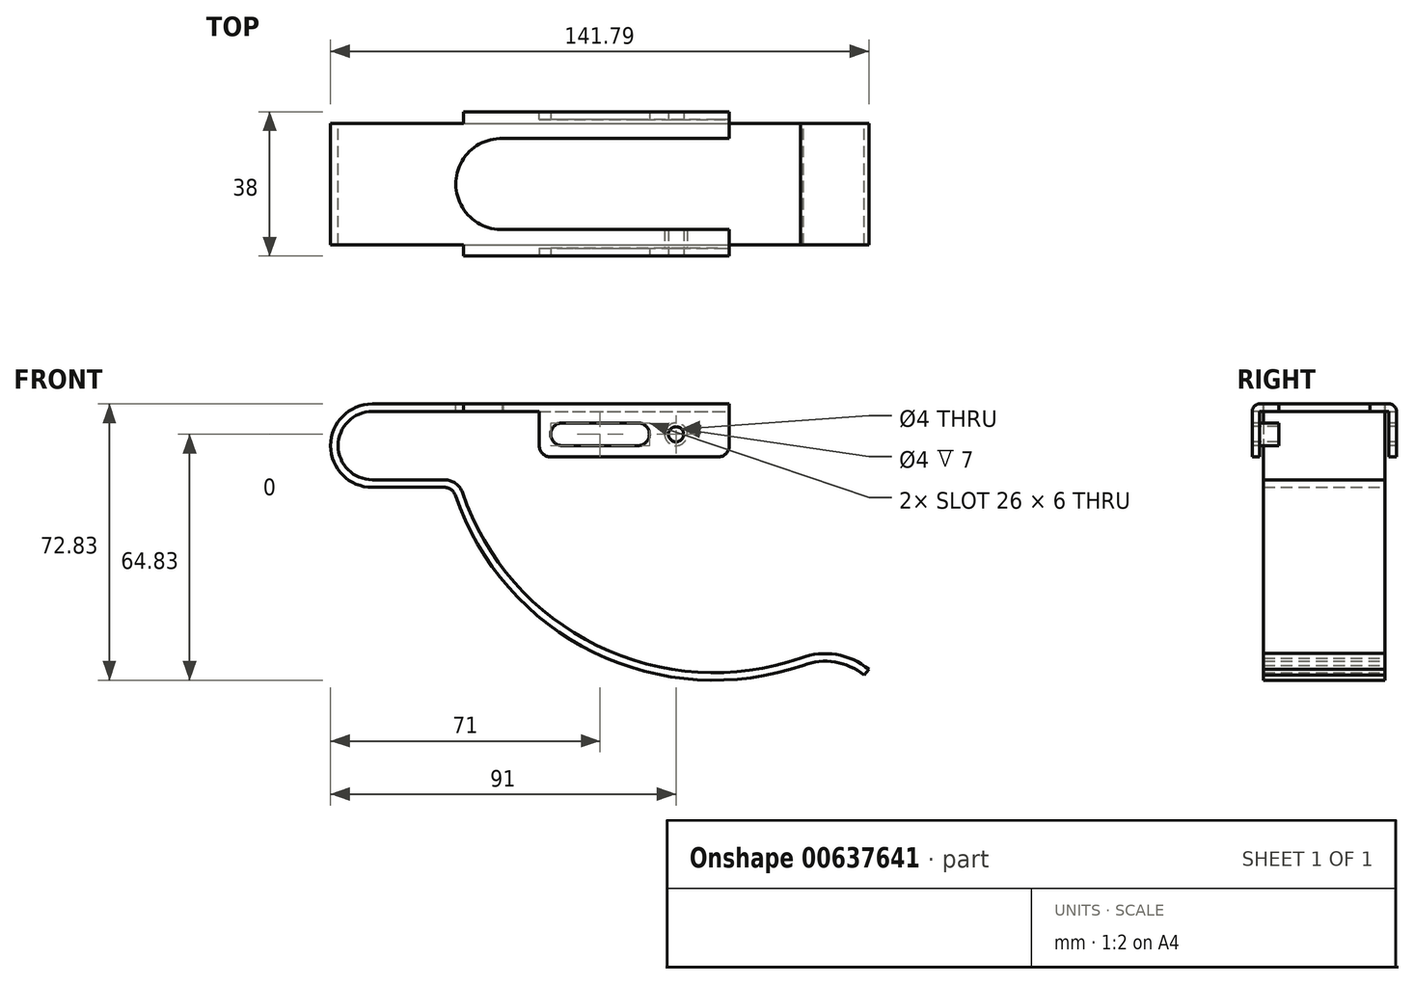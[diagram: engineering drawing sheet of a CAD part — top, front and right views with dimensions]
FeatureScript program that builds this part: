
annotation { "Feature Type Name" : "Feature", "Feature Type Description" : "" }
export const myFeature = defineFeature(function(context is Context, id is Id, definition is map)
    precondition{}
    {
        {
            var Q0;
            Q0=qCreatedBy(makeId("Front.planeOp"),FACE);
            var sketch = newSketch(context, id + "F0", { "sketchPlane" : qUnion([Q0])});
            skArc(sketch, "E0", {"start": v(0, 9) * mm, "mid": v(-9, 0) * mm, "end": v(0, -9) * mm});
            skLineSegment(sketch, "E1", {"start": v(0, 9) * mm, "end": v(94, 9) * mm});
            skLineSegment(sketch, "E2", {"start": v(0, -9) * mm, "end": v(19, -9) * mm});
            skArc(sketch, "E3", {"start": v(23.73, -12.39) * mm, "mid": v(59.23, -52.7) * mm, "end": v(112.85, -56) * mm});
            skArc(sketch, "E4", {"start": v(130.79, -59) * mm, "mid": v(122.23, -55.07) * mm, "end": v(112.85, -56) * mm});
            skPoint(sketch, "E5.visualSharp", {"position": v(22.67, -9) * mm});
            skArc(sketch, "E5.filletArc", {"start": v(23.73, -12.39) * mm, "mid": v(21.91, -9.93) * mm, "end": v(19, -9) * mm});
            skLineSegment(sketch, "E6.0", {"start": v(0, 11) * mm, "end": v(94, 11) * mm});
            skArc(sketch, "E6.1", {"start": v(0, 11) * mm, "mid": v(-11, 0) * mm, "end": v(0, -11) * mm});
            skArc(sketch, "E6.2", {"start": v(129.5, -60.53) * mm, "mid": v(121.88, -57.04) * mm, "end": v(113.53, -57.88) * mm});
            skArc(sketch, "E6.3", {"start": v(21.84, -13.03) * mm, "mid": v(58.37, -54.51) * mm, "end": v(113.53, -57.88) * mm});
            skArc(sketch, "E6.4", {"start": v(21.84, -13.03) * mm, "mid": v(20.75, -11.56) * mm, "end": v(19, -11) * mm});
            skLineSegment(sketch, "E6.5", {"start": v(0, -11) * mm, "end": v(19, -11) * mm});
            skLineSegment(sketch, "E7", {"start": v(129.5, -60.53) * mm, "end": v(130.79, -59) * mm});
            skLineSegment(sketch, "E8", {"start": v(94, 11) * mm, "end": v(94, 9) * mm});
            skLineSegment(sketch, "E9", {"start": v(130.79, -59) * mm, "end": v(133.98, -59) * mm, "construction": true});
            skSolve(sketch);
        }
        {
            var Q0;
            Q0 = qSketchRegion(id + "F0", true);
            extrude(context, id + "F1", {"entities" : qUnion([Q0]), "depth" : 16 * mm, "offsetDistance" : 25 * mm});
        }
        {
            var Q0;
            Q0=makeQuery(id+"F1.opExtrude","SWEPT_FACE",FACE,{"disambiguationData":[OSD([sQuery(id+"F0.wireOp",EDGE,"E6.0")])]});
            var sketch = newSketch(context, id + "F2", { "sketchPlane" : qUnion([Q0])});
            skLineSegment(sketch, "E10.bottom", {"start": v(24, -16) * mm, "end": v(94, -16) * mm});
            skLineSegment(sketch, "E10.top", {"start": v(24, -19) * mm, "end": v(94, -19) * mm});
            skLineSegment(sketch, "E10.left", {"start": v(24, -16) * mm, "end": v(24, -19) * mm});
            skLineSegment(sketch, "E10.right", {"start": v(94, -16) * mm, "end": v(94, -19) * mm});
            skSolve(sketch);
        }
        {
            var Q0;
            Q0 = qSketchRegion(id + "F2", true);
            extrude(context, id + "F3", {"entities" : qUnion([Q0]), "operationType" : NewBodyOperationType.ADD, "oppositeDirection" : true, "depth" : 2 * mm, "offsetDistance" : 25 * mm});
        }
        {
            var Q0;
            Q0=makeQuery(id+"F3.opExtrude","SWEPT_FACE",FACE,{"disambiguationData":[OSD([sQuery(id+"F2.wireOp",EDGE,"E10.top")])]});
            var sketch = newSketch(context, id + "F4", { "sketchPlane" : qUnion([Q0])});
            skLineSegment(sketch, "E11.bottom", {"start": v(94, 11) * mm, "end": v(44, 11) * mm});
            skLineSegment(sketch, "E11.top", {"start": v(94, -3) * mm, "end": v(44, -3) * mm});
            skLineSegment(sketch, "E11.left", {"start": v(94, 11) * mm, "end": v(94, -3) * mm});
            skLineSegment(sketch, "E11.right", {"start": v(44, 11) * mm, "end": v(44, -3) * mm});
            skSolve(sketch);
        }
        {
            var Q0;
            Q0 = qSketchRegion(id + "F4", true);
            extrude(context, id + "F5", {"entities" : qUnion([Q0]), "operationType" : NewBodyOperationType.ADD, "oppositeDirection" : true, "depth" : 2 * mm, "offsetDistance" : 25 * mm});
        }
        {
            var Q0;
            Q0=makeQuery(id+"F3.opExtrude","CAP_EDGE",EDGE,{"disambiguationData":[OSD([sQuery(id+"F2.wireOp",EDGE,"E10.top")])],"isStart":true});
            fillet(context, id + "F6", {"entities" : qUnion([Q0]), "radius" : 2 * mm, "tangentPropagation" : true, "allowEdgeOverflow" : false});
        }
        {
            var Q0;
            Q0=makeQuery(id+"F1.opExtrude","SWEPT_BODY",BODY,{"disambiguationData":[OSD([sQuery(id+"F0.wireOp",EDGE,"E0"),sQuery(id+"F0.wireOp",EDGE,"E1"),sQuery(id+"F0.wireOp",EDGE,"E2"),sQuery(id+"F0.wireOp",EDGE,"E3"),sQuery(id+"F0.wireOp",EDGE,"E4"),sQuery(id+"F0.wireOp",EDGE,"E5.filletArc"),sQuery(id+"F0.wireOp",EDGE,"E6.0"),sQuery(id+"F0.wireOp",EDGE,"E6.1"),sQuery(id+"F0.wireOp",EDGE,"E6.2"),sQuery(id+"F0.wireOp",EDGE,"E6.3"),sQuery(id+"F0.wireOp",EDGE,"E6.4"),sQuery(id+"F0.wireOp",EDGE,"E6.5"),sQuery(id+"F0.wireOp",EDGE,"E7"),sQuery(id+"F0.wireOp",EDGE,"E8")])]});
            var Q1;
            Q1=qCreatedBy(makeId("Front.planeOp"),FACE);
            mirror(context, id + "F7", {"operationType" : NewBodyOperationType.ADD, "entities" : qUnion([Q0]), "mirrorPlane" : qUnion([Q1])});
        }
        {
            var Q0;
            {var subQ0=makeQuery(id+"F3.boolean.opBoolean","MERGE",FACE,{"derivedFrom":[makeQuery(id+"F1.opExtrude","SWEPT_FACE",FACE,{"disambiguationData":[OSD([sQuery(id+"F0.wireOp",EDGE,"E6.0")])]}),makeQuery(id+"F3.opExtrude","CAP_FACE",FACE,{"disambiguationData":[OSD([sQuery(id+"F2.wireOp",EDGE,"E10.bottom"),sQuery(id+"F2.wireOp",EDGE,"E10.top"),sQuery(id+"F2.wireOp",EDGE,"E10.left"),sQuery(id+"F2.wireOp",EDGE,"E10.right")])],"isStart":true})]});Q0=makeQuery(id+"F7.boolean.opBoolean","MERGE",FACE,{"derivedFrom":[subQ0,makeQuery(id+"F7.opPattern","COPY",FACE,{"derivedFrom":subQ0,"instanceName":"1"})]});}
            var sketch = newSketch(context, id + "F8", { "sketchPlane" : qUnion([Q0])});
            skArc(sketch, "E12", {"start": v(34.3, 12) * mm, "mid": v(22, -0.11) * mm, "end": v(34.54, -11.99) * mm});
            skLineSegment(sketch, "E13", {"start": v(33.7, 12) * mm, "end": v(94, 12) * mm});
            skLineSegment(sketch, "E14", {"start": v(34.54, -11.99) * mm, "end": v(94, -11.99) * mm});
            skSolve(sketch);
        }
        {
            var Q0;
            Q0 = qSketchRegion(id + "F8", true);
            var Q1;
            {var subQ0=sQuery(id+"F8.wireOp",EDGE,"E14");Q1=makeQuery(id+"F8.imprint","IMPRINT",FACE,{"disambiguationData":[TD([[makeQuery(id+"F8.imprint","IMPRINT",EDGE,{"derivedFrom":subQ0}),1.0]])]});}
            extrude(context, id + "F9", {"entities" : qUnion([Q0, Q1]), "operationType" : NewBodyOperationType.REMOVE, "oppositeDirection" : true, "depth" : 2 * mm, "offsetDistance" : 25 * mm});
        }
        {
            var Q0;
            Q0=makeQuery(id+"F5.boolean.opBoolean","MERGE",FACE,{"derivedFrom":[makeQuery(id+"F3.opExtrude","SWEPT_FACE",FACE,{"disambiguationData":[OSD([sQuery(id+"F2.wireOp",EDGE,"E10.top")])]}),makeQuery(id+"F5.opExtrude","CAP_FACE",FACE,{"disambiguationData":[OSD([sQuery(id+"F4.wireOp",EDGE,"E11.bottom"),sQuery(id+"F4.wireOp",EDGE,"E11.top"),sQuery(id+"F4.wireOp",EDGE,"E11.left"),sQuery(id+"F4.wireOp",EDGE,"E11.right")])],"isStart":true})]});
            var sketch = newSketch(context, id + "F10", { "sketchPlane" : qUnion([Q0])});
            skLineSegment(sketch, "E15", {"start": v(50, 3) * mm, "end": v(70, 3) * mm});
            skPoint(sketch, "E15.startSnap0", {"position": v(44, 3) * mm});
            skArc(sketch, "E16.0.startCap", {"start": v(50, 0) * mm, "mid": v(47, 3) * mm, "end": v(50, 6) * mm});
            skArc(sketch, "E16.0.endCap", {"start": v(70, 6) * mm, "mid": v(73, 3) * mm, "end": v(70, 0) * mm});
            skLineSegment(sketch, "E16.0.left", {"start": v(50, 6) * mm, "end": v(70, 6) * mm});
            skLineSegment(sketch, "E16.0.right", {"start": v(50, 0) * mm, "end": v(70, 0) * mm});
            skSolve(sketch);
        }
        {
            var Q0;
            Q0 = qSketchRegion(id + "F10", true);
            extrude(context, id + "F11", {"entities" : qUnion([Q0]), "operationType" : NewBodyOperationType.REMOVE, "endBound" : BoundingType.THROUGH_ALL, "oppositeDirection" : true, "depth" : 25 * mm, "offsetDistance" : 25 * mm});
        }
        {
            var Q0;
            Q0=makeQuery(id+"F5.boolean.opBoolean","MERGE",FACE,{"derivedFrom":[makeQuery(id+"F3.opExtrude","SWEPT_FACE",FACE,{"disambiguationData":[OSD([sQuery(id+"F2.wireOp",EDGE,"E10.top")])]}),makeQuery(id+"F5.opExtrude","CAP_FACE",FACE,{"disambiguationData":[OSD([sQuery(id+"F4.wireOp",EDGE,"E11.bottom"),sQuery(id+"F4.wireOp",EDGE,"E11.top"),sQuery(id+"F4.wireOp",EDGE,"E11.left"),sQuery(id+"F4.wireOp",EDGE,"E11.right")])],"isStart":true})]});
            var sketch = newSketch(context, id + "F12", { "sketchPlane" : qUnion([Q0])});
            skPoint(sketch, "E17", {"position": v(80, 3) * mm});
            skSolve(sketch);
        }
        {
            var Q0;
            Q0=sQuery(id+"F12.wireOp",VERTEX,"E17");
            var Q1;
            Q1=makeQuery(id+"F1.opExtrude","SWEPT_BODY",BODY,{"disambiguationData":[OSD([sQuery(id+"F0.wireOp",EDGE,"E0"),sQuery(id+"F0.wireOp",EDGE,"E1"),sQuery(id+"F0.wireOp",EDGE,"E2"),sQuery(id+"F0.wireOp",EDGE,"E3"),sQuery(id+"F0.wireOp",EDGE,"E4"),sQuery(id+"F0.wireOp",EDGE,"E5.filletArc"),sQuery(id+"F0.wireOp",EDGE,"E6.0"),sQuery(id+"F0.wireOp",EDGE,"E6.1"),sQuery(id+"F0.wireOp",EDGE,"E6.2"),sQuery(id+"F0.wireOp",EDGE,"E6.3"),sQuery(id+"F0.wireOp",EDGE,"E6.4"),sQuery(id+"F0.wireOp",EDGE,"E6.5"),sQuery(id+"F0.wireOp",EDGE,"E7"),sQuery(id+"F0.wireOp",EDGE,"E8")])]});
            hole(context, id + "F13", {"style" : HoleStyle.SIMPLE, "endStyle" : HoleEndStyle.THROUGH, "holeDiameter" : 4 * mm, "majorDiameter" : 5 * mm, "isTappedThrough" : true, "tappedDepth" : 12 * mm, "tapClearance" : 3, "locations" : qUnion([Q0]), "scope" : qUnion([Q1])});
        }
        {
            var Q0;
            Q0=makeQuery(id+"F5.opExtrude","CAP_FACE",FACE,{"disambiguationData":[OSD([sQuery(id+"F4.wireOp",EDGE,"E11.bottom"),sQuery(id+"F4.wireOp",EDGE,"E11.top"),sQuery(id+"F4.wireOp",EDGE,"E11.left"),sQuery(id+"F4.wireOp",EDGE,"E11.right")])],"isStart":false});
            var sketch = newSketch(context, id + "F14", { "sketchPlane" : qUnion([Q0])});
            skCircle(sketch, "E18.0", {"center": v(-80, 3) * mm, "radius": 2 * mm});
            skCircle(sketch, "E19.0", {"center": v(-80, 3) * mm, "radius": 3 * mm});
            skSolve(sketch);
        }
        {
            var Q0;
            Q0 = qSketchRegion(id + "F14", true);
            extrude(context, id + "F15", {"entities" : qUnion([Q0]), "operationType" : NewBodyOperationType.ADD, "depth" : 5 * mm, "offsetDistance" : 25 * mm});
        }
        {
            var Q0;
            Q0=makeQuery(id+"F7.opPattern","COPY",EDGE,{"derivedFrom":makeQuery(id+"F5.opExtrude","SWEPT_EDGE",EDGE,{"disambiguationData":[OSD([sQuery(id+"F4.wireOp",EDGE,"E11.top"),sQuery(id+"F4.wireOp",EDGE,"E11.right")])]}),"instanceName":"1"});
            var Q1;
            Q1=makeQuery(id+"F5.opExtrude","SWEPT_EDGE",EDGE,{"disambiguationData":[OSD([sQuery(id+"F4.wireOp",EDGE,"E11.top"),sQuery(id+"F4.wireOp",EDGE,"E11.right")])]});
            var Q2;
            Q2=makeQuery(id+"F7.opPattern","COPY",EDGE,{"derivedFrom":makeQuery(id+"F5.opExtrude","SWEPT_EDGE",EDGE,{"disambiguationData":[OSD([sQuery(id+"F4.wireOp",EDGE,"E11.top"),sQuery(id+"F4.wireOp",EDGE,"E11.left")])]}),"instanceName":"1"});
            var Q3;
            Q3=makeQuery(id+"F5.opExtrude","SWEPT_EDGE",EDGE,{"disambiguationData":[OSD([sQuery(id+"F4.wireOp",EDGE,"E11.top"),sQuery(id+"F4.wireOp",EDGE,"E11.left")])]});
            fillet(context, id + "F16", {"entities" : qUnion([Q0, Q1, Q2, Q3]), "radius" : 3 * mm, "tangentPropagation" : true, "allowEdgeOverflow" : false});
        }
    });
